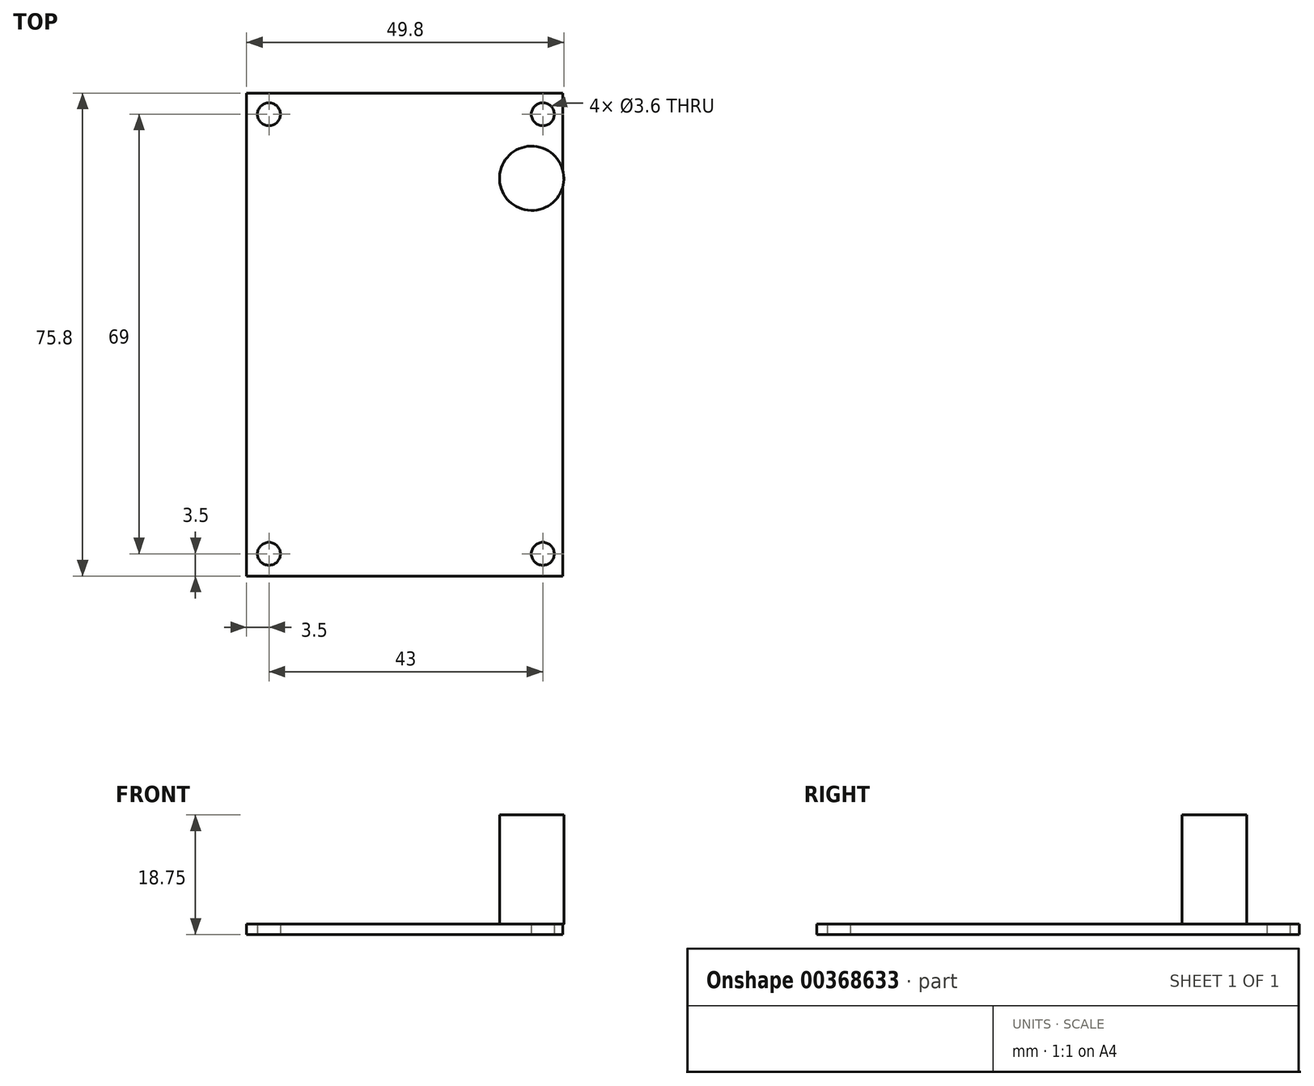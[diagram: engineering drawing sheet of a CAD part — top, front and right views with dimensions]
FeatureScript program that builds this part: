
annotation { "Feature Type Name" : "Feature", "Feature Type Description" : "" }
export const myFeature = defineFeature(function(context is Context, id is Id, definition is map)
    precondition{}
    {
        {
            var Q0;
            Q0=qCreatedBy(makeId("Top.planeOp"),FACE);
            var sketch = newSketch(context, id + "F0", { "sketchPlane" : qUnion([Q0])});
            skLineSegment(sketch, "E0.bottom", {"start": v(-24.8, 37.9) * mm, "end": v(24.8, 37.9) * mm});
            skLineSegment(sketch, "E0.top", {"start": v(-24.8, -37.9) * mm, "end": v(24.8, -37.9) * mm});
            skLineSegment(sketch, "E0.left", {"start": v(-24.8, 37.9) * mm, "end": v(-24.8, -37.9) * mm});
            skLineSegment(sketch, "E0.right", {"start": v(24.8, 37.9) * mm, "end": v(24.8, -37.9) * mm});
            skPoint(sketch, "E0.middle", {"position": v(0, 0) * mm});
            skCircle(sketch, "E1", {"center": v(-21.3, 34.6) * mm, "radius": 1.8 * mm});
            skCircle(sketch, "E2", {"center": v(21.7, 34.6) * mm, "radius": 1.8 * mm});
            skCircle(sketch, "E3", {"center": v(21.7, -34.4) * mm, "radius": 1.8 * mm});
            skCircle(sketch, "E4", {"center": v(-21.3, -34.4) * mm, "radius": 1.8 * mm});
            skLineSegment(sketch, "E5", {"start": v(-21.3, 34.6) * mm, "end": v(-24.8, 34.6) * mm, "construction": true});
            skLineSegment(sketch, "E6", {"start": v(-21.3, -34.4) * mm, "end": v(-24.8, -34.4) * mm, "construction": true});
            skLineSegment(sketch, "E7", {"start": v(-21.3, 34.6) * mm, "end": v(21.7, 34.6) * mm, "construction": true});
            skLineSegment(sketch, "E8", {"start": v(21.7, 34.6) * mm, "end": v(24.8, 34.6) * mm, "construction": true});
            skLineSegment(sketch, "E9", {"start": v(21.7, -34.4) * mm, "end": v(24.8, -34.4) * mm, "construction": true});
            skLineSegment(sketch, "E10", {"start": v(-21.3, -34.4) * mm, "end": v(21.7, -34.4) * mm, "construction": true});
            skLineSegment(sketch, "E11", {"start": v(-21.3, -34.4) * mm, "end": v(-21.3, -37.9) * mm, "construction": true});
            skLineSegment(sketch, "E12", {"start": v(21.7, -34.4) * mm, "end": v(21.7, -37.9) * mm, "construction": true});
            skLineSegment(sketch, "E13", {"start": v(-21.3, 34.6) * mm, "end": v(-21.3, 37.9) * mm, "construction": true});
            skLineSegment(sketch, "E14", {"start": v(21.7, 34.6) * mm, "end": v(21.7, 37.9) * mm, "construction": true});
            skLineSegment(sketch, "E15", {"start": v(-21.3, 34.6) * mm, "end": v(-21.3, -34.4) * mm, "construction": true});
            skLineSegment(sketch, "E16", {"start": v(21.7, 34.6) * mm, "end": v(21.7, -34.4) * mm, "construction": true});
            skSolve(sketch);
        }
        {
            var Q0;
            Q0=makeQuery(id+"F0.imprint","IMPRINT",FACE,{"disambiguationData":[TD([[makeQuery(id+"F0.imprint","IMPRINT",EDGE,{"derivedFrom":sQuery(id+"F0.wireOp",EDGE,"E0.bottom")}),-1.0]])]});
            extrude(context, id + "F1", {"entities" : qUnion([Q0]), "depth" : 1.6 * mm});
        }
        {
            var Q0;
            Q0=makeQuery(id+"F1.opExtrude","CAP_FACE",FACE,{"disambiguationData":[OSD([sQuery(id+"F0.wireOp",EDGE,"E0.bottom"),sQuery(id+"F0.wireOp",EDGE,"E0.top"),sQuery(id+"F0.wireOp",EDGE,"E0.left"),sQuery(id+"F0.wireOp",EDGE,"E0.right"),sQuery(id+"F0.wireOp",EDGE,"E1"),sQuery(id+"F0.wireOp",EDGE,"E2"),sQuery(id+"F0.wireOp",EDGE,"E3"),sQuery(id+"F0.wireOp",EDGE,"E4")])],"isStart":false});
            var sketch = newSketch(context, id + "F2", { "sketchPlane" : qUnion([Q0])});
            skCircle(sketch, "E17", {"center": v(19.95, 24.55) * mm, "radius": 5.05 * mm});
            skLineSegment(sketch, "E18", {"start": v(19.95, 29.6) * mm, "end": v(19.87, 37.9) * mm, "construction": true});
            skSolve(sketch);
        }
        {
            var Q0;
            {var subQ0=sQuery(id+"F2.wireOp",EDGE,"E17");var subQ1=makeQuery(id+"F1.opExtrude","CAP_EDGE",EDGE,{"disambiguationData":[OSD([sQuery(id+"F0.wireOp",EDGE,"E0.right")])],"isStart":false});var subQ2=makeQuery(id+"F2.imprint","INTERSECT",VERTEX,{"disambiguationData":[OD(0.0)],"derivedFrom":[subQ1,subQ0]});Q0=makeQuery(id+"F2.imprint","IMPRINT",FACE,{"disambiguationData":[TD([[makeQuery(id+"F2.imprint","IMPRINT",EDGE,{"disambiguationData":[TD([[subQ2,1.0]])],"derivedFrom":subQ0}),1.0]])]});}
            var Q1;
            {var subQ0=sQuery(id+"F2.wireOp",EDGE,"E17");var subQ1=makeQuery(id+"F1.opExtrude","CAP_EDGE",EDGE,{"disambiguationData":[OSD([sQuery(id+"F0.wireOp",EDGE,"E0.right")])],"isStart":false});var subQ2=makeQuery(id+"F2.imprint","INTERSECT",VERTEX,{"disambiguationData":[OD(0.0)],"derivedFrom":[subQ1,subQ0]});Q1=makeQuery(id+"F2.imprint","IMPRINT",FACE,{"disambiguationData":[TD([[makeQuery(id+"F2.imprint","IMPRINT",EDGE,{"disambiguationData":[TD([[subQ2,-1.0]])],"derivedFrom":subQ0}),1.0]])]});}
            extrude(context, id + "F3", {"entities" : qUnion([Q0, Q1]), "operationType" : NewBodyOperationType.ADD, "depth" : 17.15 * mm});
        }
    });
